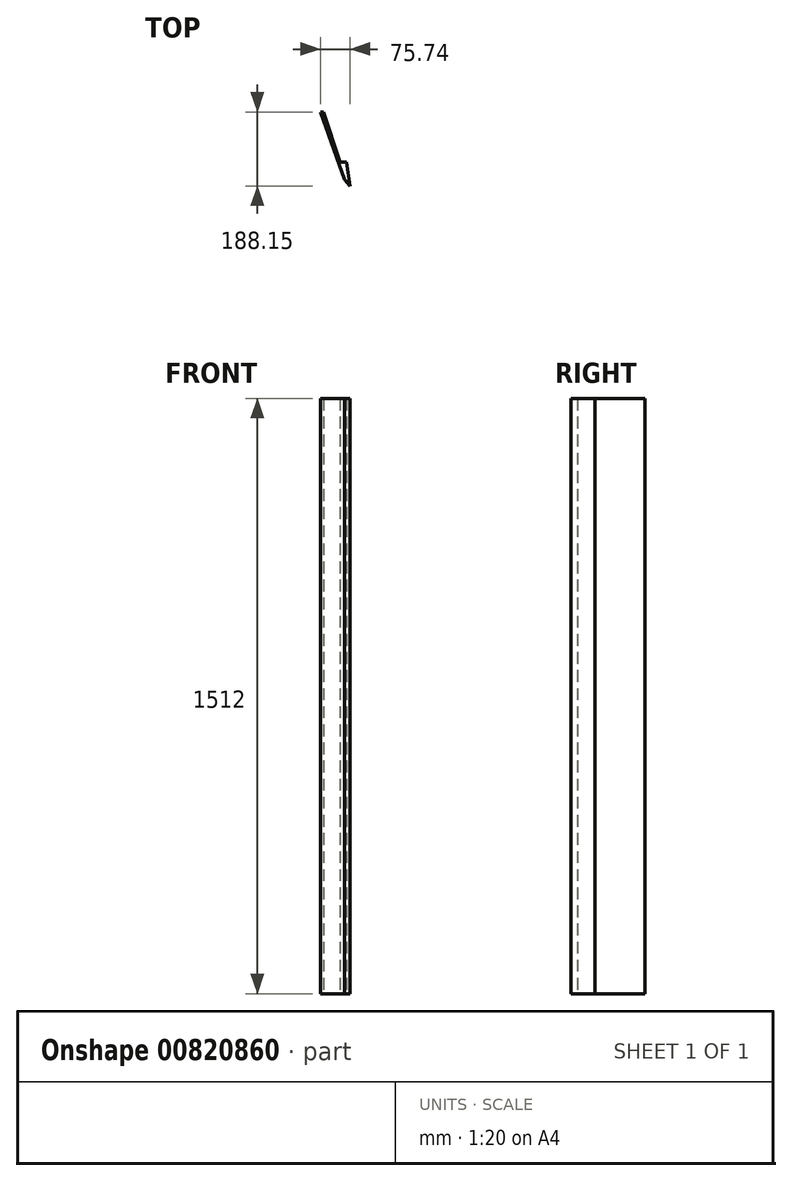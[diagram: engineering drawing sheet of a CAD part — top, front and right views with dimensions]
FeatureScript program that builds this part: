
annotation { "Feature Type Name" : "Feature", "Feature Type Description" : "" }
export const myFeature = defineFeature(function(context is Context, id is Id, definition is map)
    precondition{}
    {
        {
            var Q0;
            Q0=qCreatedBy(makeId("Top.planeOp"),FACE);
            var sketch = newSketch(context, id + "F0", { "sketchPlane" : qUnion([Q0])});
            skLineSegment(sketch, "E0", {"start": v(-26.44, -52.5) * mm, "end": v(-87.94, 119.88) * mm});
            skLineSegment(sketch, "E1", {"start": v(-87.94, 119.88) * mm, "end": v(-79.8, 119.88) * mm});
            skLineSegment(sketch, "E2", {"start": v(-79.8, 119.88) * mm, "end": v(-37.6, -7.37) * mm});
            skLineSegment(sketch, "E3", {"start": v(-37.6, -7.37) * mm, "end": v(-21.56, -7.37) * mm});
            skLineSegment(sketch, "E4", {"start": v(-21.56, -7.37) * mm, "end": v(-12.2, -68.27) * mm});
            skLineSegment(sketch, "E5", {"start": v(-12.2, -68.27) * mm, "end": v(-26.44, -52.5) * mm});
            skSolve(sketch);
        }
        {
            var Q0;
            Q0=makeQuery(id+"F0.imprint","IMPRINT",FACE,{"disambiguationData":[TD([[makeQuery(id+"F0.imprint","IMPRINT",EDGE,{"derivedFrom":sQuery(id+"F0.wireOp",EDGE,"E0")}),-1.0]])]});
            extrude(context, id + "F1", {"entities" : qUnion([Q0]), "depth" : 1512 * mm, "offsetDistance" : 25 * mm});
        }
    });
